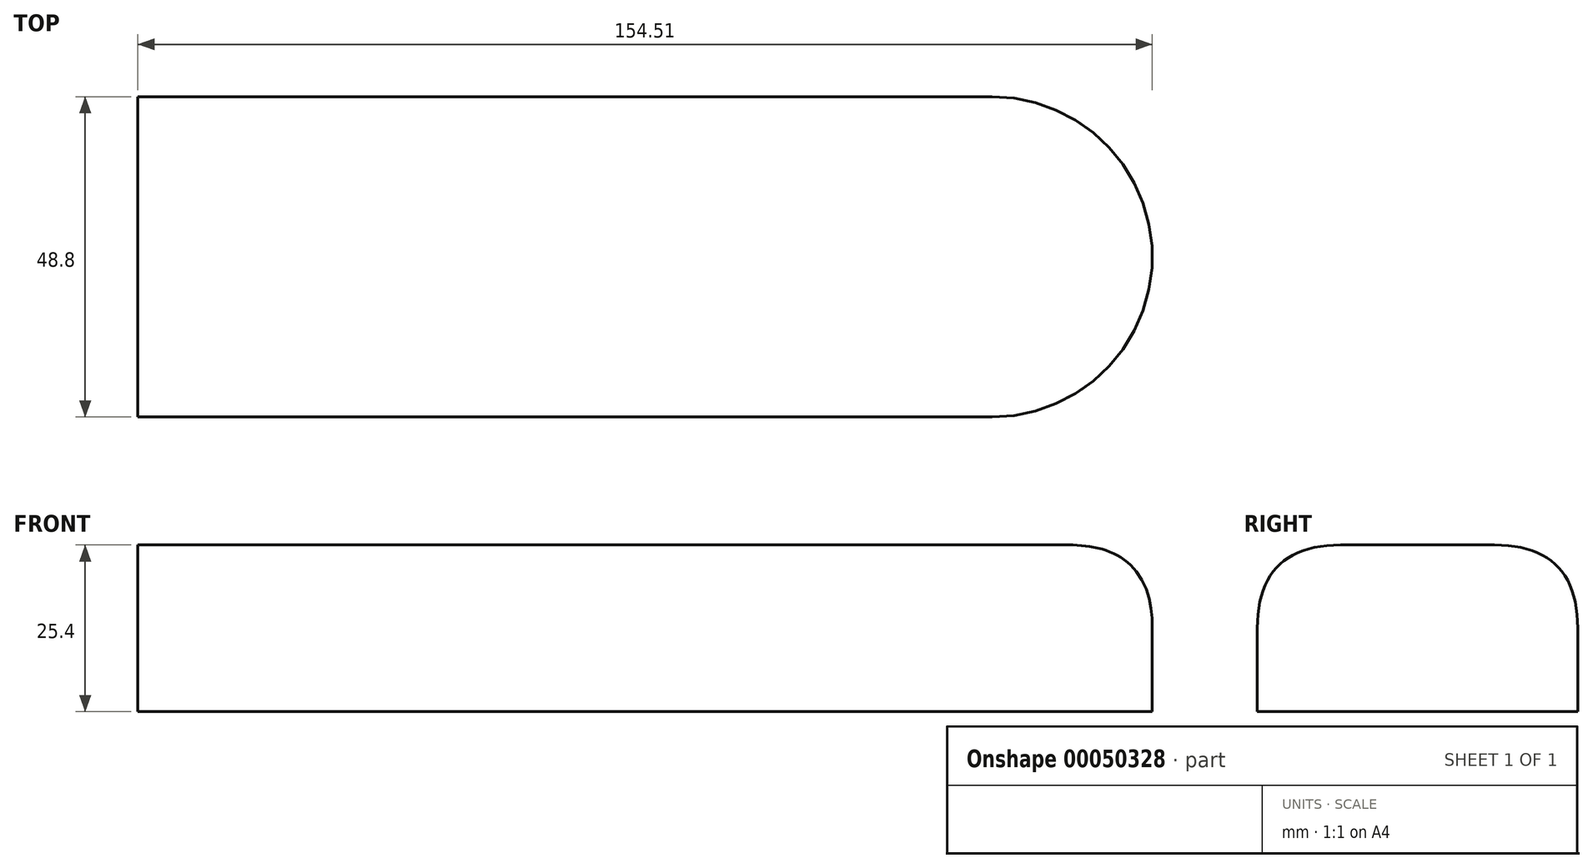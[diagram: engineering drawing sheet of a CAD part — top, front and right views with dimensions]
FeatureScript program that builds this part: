
annotation { "Feature Type Name" : "Feature", "Feature Type Description" : "" }
export const myFeature = defineFeature(function(context is Context, id is Id, definition is map)
    precondition{}
    {
        {
            var Q0;
            Q0=qCreatedBy(makeId("Top.planeOp"),FACE);
            var sketch = newSketch(context, id + "F0", { "sketchPlane" : qUnion([Q0])});
            skLineSegment(sketch, "E0.rect.bottom", {"start": v(0, 0) * mm, "end": v(-1.57, 0) * mm});
            skLineSegment(sketch, "E0.rect.top", {"start": v(0, 2.62) * mm, "end": v(-1.57, 2.62) * mm});
            skLineSegment(sketch, "E0.rect.left", {"start": v(0, 0) * mm, "end": v(0, 2.62) * mm});
            skLineSegment(sketch, "E0.rect.right", {"start": v(-1.57, 0) * mm, "end": v(-1.57, 2.62) * mm});
            skPoint(sketch, "E0.rect.middle", {"position": v(-0.79, 1.31) * mm});
            skLineSegment(sketch, "E1.rect.bottom", {"start": v(65.06, -24.4) * mm, "end": v(-65.06, -24.4) * mm});
            skLineSegment(sketch, "E1.rect.top", {"start": v(65.06, 24.4) * mm, "end": v(-65.06, 24.4) * mm});
            skLineSegment(sketch, "E1.rect.right", {"start": v(-65.06, -24.4) * mm, "end": v(-65.06, 24.4) * mm});
            skPoint(sketch, "E1.rect.middle", {"position": v(0, 0) * mm});
            skArc(sketch, "E2", {"start": v(65.06, -24.4) * mm, "mid": v(89.45, 0) * mm, "end": v(65.06, 24.4) * mm});
            skSolve(sketch);
        }
        {
            var Q0;
            Q0=makeQuery(id+"F0.imprint","IMPRINT",FACE,{"disambiguationData":[TD([[makeQuery(id+"F0.imprint","IMPRINT",EDGE,{"derivedFrom":sQuery(id+"F0.wireOp",EDGE,"E0.rect.bottom")}),1.0]])]});
            var Q1;
            Q1=makeQuery(id+"F0.imprint","IMPRINT",FACE,{"disambiguationData":[TD([[makeQuery(id+"F0.imprint","IMPRINT",EDGE,{"derivedFrom":sQuery(id+"F0.wireOp",EDGE,"E0.rect.bottom")}),-1.0]])]});
            extrude(context, id + "F1", {"entities" : qUnion([Q0, Q1]), "depth" : 25.4 * mm});
        }
        {
            var Q0;
            Q0=makeQuery(id+"F1.opExtrude","CAP_EDGE",EDGE,{"disambiguationData":[OSD([sQuery(id+"F0.wireOp",EDGE,"E2")])],"isStart":false});
            fillet(context, id + "F2", {"entities" : qUnion([Q0]), "radius" : 12.7 * mm, "tangentPropagation" : true, "rho" : 0.5, "crossSection" : FilletCrossSection.CONIC, "allowEdgeOverflow" : false});
        }
        {
            var Q0;
            Q0=makeQuery(id+"F1.opExtrude","CAP_FACE",FACE,{"disambiguationData":[OSD([sQuery(id+"F0.wireOp",EDGE,"E1.rect.bottom"),sQuery(id+"F0.wireOp",EDGE,"E1.rect.top"),sQuery(id+"F0.wireOp",EDGE,"E1.rect.right"),sQuery(id+"F0.wireOp",EDGE,"E2")])],"isStart":false});
            var sketch = newSketch(context, id + "F3", { "sketchPlane" : qUnion([Q0])});
            skCircle(sketch, "E3", {"center": v(65.06, 0) * mm, "radius": 12.52 * mm});
            skCircle(sketch, "E4", {"center": v(65.06, 0) * mm, "radius": 8.82 * mm});
            skLineSegment(sketch, "E5", {"start": v(52.53, 24.4) * mm, "end": v(52.53, -23.87) * mm});
            skSolve(sketch);
        }
        {
            var Q0;
            Q0=sQuery(id+"F3.wireOp",EDGE,"E3");
            var Q1;
            Q1=sQuery(id+"F3.wireOp",EDGE,"E4");
            extrude(context, id + "F4", {"bodyType" : ToolBodyType.SURFACE, "surfaceEntities" : qUnion([Q0, Q1]), "depth" : 25.4 * mm});
        }
    });
